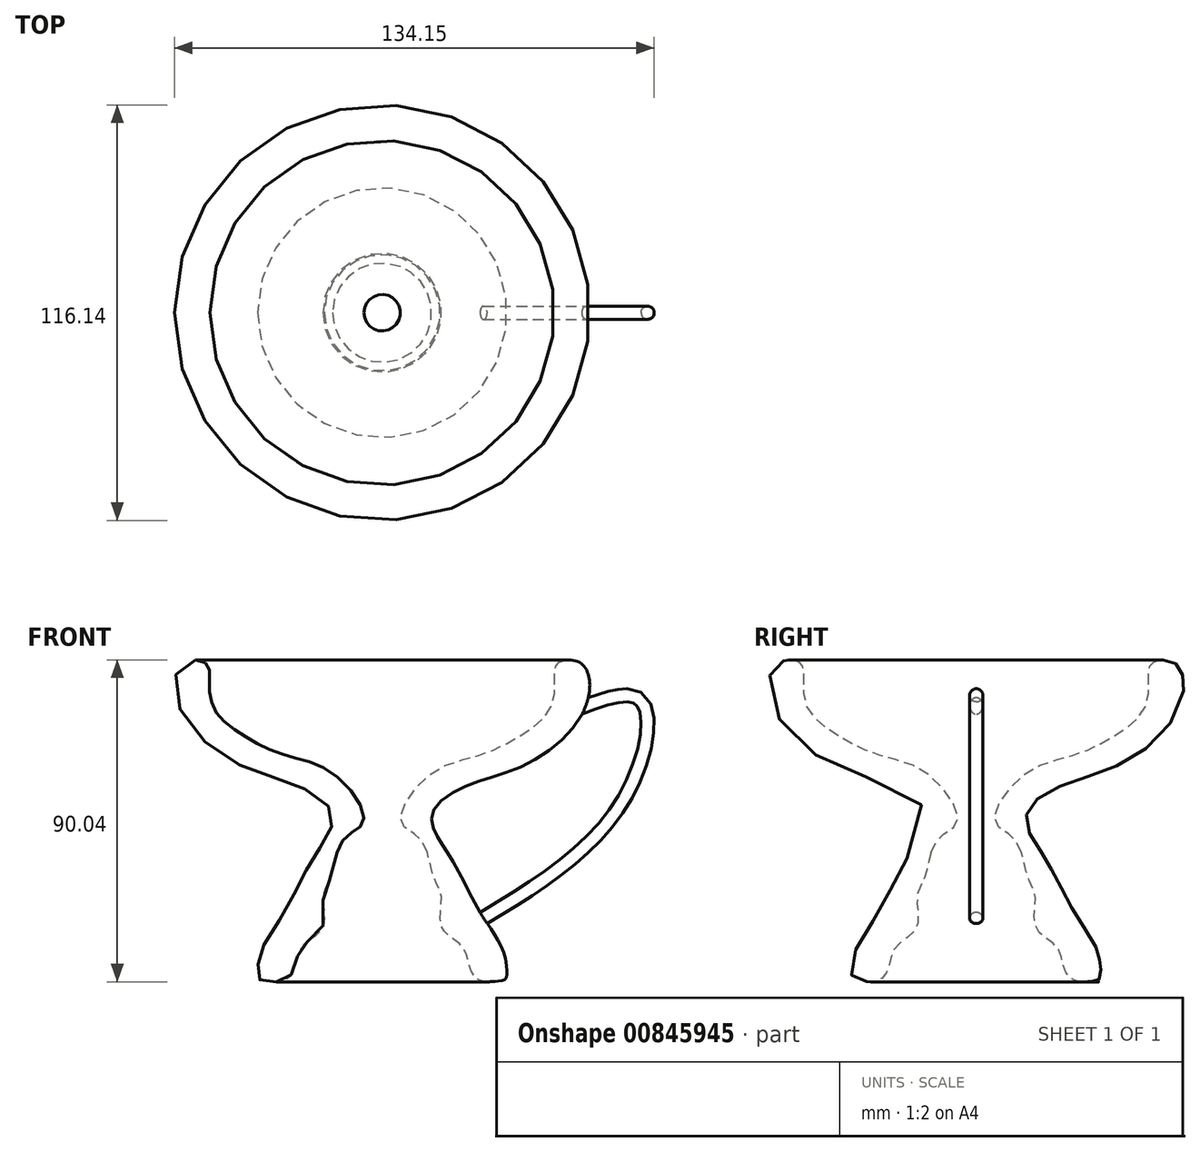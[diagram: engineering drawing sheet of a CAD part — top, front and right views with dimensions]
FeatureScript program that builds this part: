
annotation { "Feature Type Name" : "Feature", "Feature Type Description" : "" }
export const myFeature = defineFeature(function(context is Context, id is Id, definition is map)
    precondition{}
    {
        {
            var Q0;
            Q0=qCreatedBy(makeId("Front.planeOp"),FACE);
            var sketch = newSketch(context, id + "F0", { "sketchPlane" : qUnion([Q0])});
            skFitSpline(sketch, "E0", {"points": [v(50.7, 43.94) * mm, v(51.33, 31.25) * mm, v(35.26, 16.03) * mm, v(19.83, 10.53) * mm, v(9.68, 3.98) * mm, v(9.04, -1.73) * mm, v(13.06, -8.7) * mm, v(17.5, -16.53) * mm, v(22.57, -26.05) * mm, v(28.28, -35.35) * mm, v(29.55, -40.42) * mm, v(29.34, -44.02) * mm, v(27.23, -44.65) * mm, v(22.57, -44.65) * mm, v(19.83, -42.12) * mm, v(18.35, -37.25) * mm, v(16.23, -34.08) * mm, v(11.37, -29.43) * mm, v(11.37, -21.18) * mm, v(9.25, -15.69) * mm, v(5.45, -4.9) * mm, v(0, 0) * mm, v(8.4, 13.28) * mm, v(22.15, 18.57) * mm, v(32.94, 23.64) * mm, v(41.18, 30.4) * mm, v(43.08, 38.02) * mm, v(43.93, 44.15) * mm, v(50.7, 43.94) * mm]});
            skLineSegment(sketch, "E1", {"start": v(-5.2, 51.31) * mm, "end": v(-5.2, -48.98) * mm});
            skSolve(sketch);
        }
        {
            var Q0;
            Q0=makeQuery(id+"F0.imprint","IMPRINT",FACE,{"disambiguationData":[TD([[makeQuery(id+"F0.imprint","IMPRINT",EDGE,{"derivedFrom":sQuery(id+"F0.wireOp",EDGE,"E0")}),-1.0]])]});
            var Q1;
            Q1=sQuery(id+"F0.wireOp",EDGE,"E1");
            revolve(context, id + "F1", {"surfaceOperationType" : NewSurfaceOperationType.NEW, "entities" : qUnion([Q0]), "axis" : qUnion([Q1]), "revolveType" : RevolveType.FULL});
        }
        {
            var Q0;
            Q0=qCreatedBy(makeId("Front.planeOp"),FACE);
            var sketch = newSketch(context, id + "F2", { "sketchPlane" : qUnion([Q0])});
            skFitSpline(sketch, "E2", {"points": [v(48.8, 31.2) * mm, v(67.12, 33.87) * mm, v(62.14, 5.78) * mm, v(22.14, -27.65) * mm], "startDerivative": vector(88.61, 34.49) * mm, "endDerivative": vector(-109.77, -66.44) * mm});
            skSolve(sketch);
        }
        {
            var Q0;
            Q0=sQuery(id+"F2.wireOp",EDGE,"E2");
            var Q1;
            Q1=sQuery(id+"F2.wireOp",VERTEX,"E2.end");
            cPlane(context, id + "F3", {"entities" : qUnion([Q0, Q1]), "cplaneType" : CPlaneType.CURVE_POINT, "offset" : 25.4 * mm, "width" : 152.4 * mm, "height" : 152.4 * mm});
        }
        {
            var Q0;
            Q0=qCreatedBy(id+"F3.planeOp",FACE);
            var sketch = newSketch(context, id + "F4", { "sketchPlane" : qUnion([Q0])});
            skCircle(sketch, "E3", {"center": v(0, -35.12) * mm, "radius": 1.84 * mm});
            skSolve(sketch);
        }
        {
            var Q0;
            Q0=makeQuery(id+"F4.imprint","IMPRINT",FACE,{"disambiguationData":[TD([[makeQuery(id+"F4.imprint","IMPRINT",EDGE,{"derivedFrom":sQuery(id+"F4.wireOp",EDGE,"E3")}),1.0]])]});
            var Q1;
            Q1=sQuery(id+"F2.wireOp",EDGE,"E2");
            sweep(context, id + "F5", {"operationType" : NewBodyOperationType.ADD, "profiles" : qUnion([Q0]), "path" : qUnion([Q1])});
        }
    });
